# Revit family: Urinal-Hybrid-Sloan-HYB-4000
name_source: partatom
category: Plumbing Fixtures
revit_build: Autodesk Revit 2014 (Build: 20130308_1515(x64)
units: mm (PartAtom-declared; Revit-internal decimal feet)

## types (1)
- HYB-4000
    ADA Compliant = Yes
    Assembly Code = D2010210
    CW Connection = No
    CWFU = 0
    Default Elevation = 24"
    Description = Complete Vitreous China Hybrid Urinal
    Fixture Color = White
    Fixture Material = Vitreous China-Sloan-White
    Flush Choice = Hybrid
    Flush Volume and Flow Rates = Waterfree
    HW Connection = No
    HWFU = 0
    Height = 22 5/8"
    Length = 14"
    Manufacturer = Sloan
    Model = HYB-4000
    Mounting = Wall Hung
    Order Code = 1004020
    Price = Prices may vary. Please consult Sloan Rep for most up-to-date price list.
    Product Documentation Link = https://specifications.sloan.com
    Product URL = https://www.sloan.com
    Revised Date = 2/3/2017
    Spud Location = Not Applicable
    URL = http://www.sloan.com
    Vent Connection = No
    WFU = 5
    Warranty = 3 Year (Limited)
    Waste Connection = Yes
    Waste Connection Diameter = 2"
    Waste Connection Height = 17"
    Waste Connection Radius = 1"
    Width = 15 3/8"

## geometry (parser evidence)
native form markers: Sweep x2
no freeform markers — native parametric forms only
